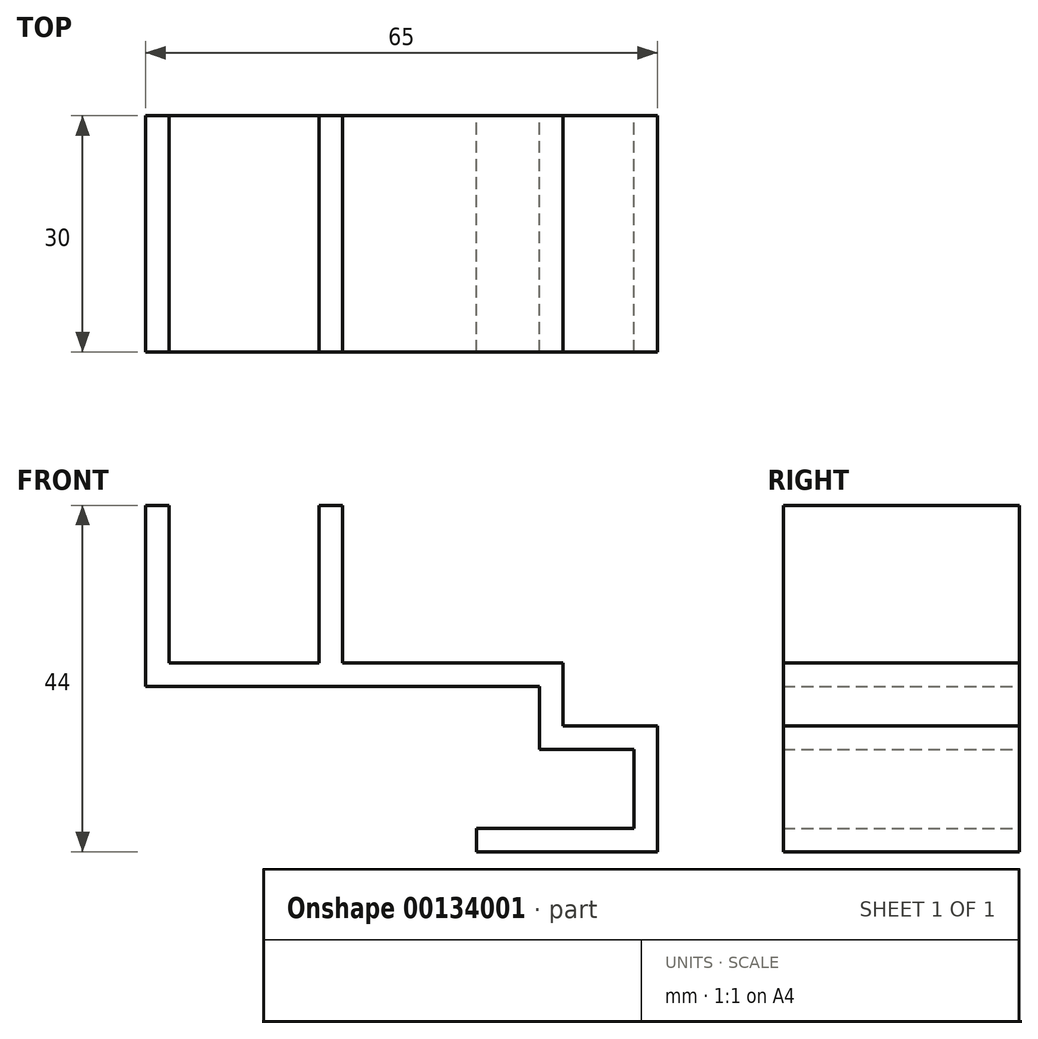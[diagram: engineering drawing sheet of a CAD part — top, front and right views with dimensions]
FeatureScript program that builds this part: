
annotation { "Feature Type Name" : "Feature", "Feature Type Description" : "" }
export const myFeature = defineFeature(function(context is Context, id is Id, definition is map)
    precondition{}
    {
        {
            var Q0;
            Q0=qCreatedBy(makeId("Front.planeOp"),FACE);
            var sketch = newSketch(context, id + "F0", { "sketchPlane" : qUnion([Q0])});
            skLineSegment(sketch, "E0.bottom", {"start": v(0, 0) * mm, "end": v(3, 0) * mm});
            skLineSegment(sketch, "E0.top", {"start": v(0, 23) * mm, "end": v(3, 23) * mm});
            skLineSegment(sketch, "E0.left", {"start": v(0, 0) * mm, "end": v(0, 23) * mm});
            skLineSegment(sketch, "E0.right", {"start": v(3, 0) * mm, "end": v(3, 23) * mm});
            skLineSegment(sketch, "E1.bottom", {"start": v(0, 0) * mm, "end": v(50, 0) * mm});
            skLineSegment(sketch, "E1.top", {"start": v(0, 3) * mm, "end": v(50, 3) * mm});
            skLineSegment(sketch, "E1.left", {"start": v(0, 0) * mm, "end": v(0, 3) * mm});
            skLineSegment(sketch, "E1.right", {"start": v(50, 0) * mm, "end": v(50, 3) * mm});
            skLineSegment(sketch, "E2.bottom", {"start": v(50, 3) * mm, "end": v(53, 3) * mm});
            skLineSegment(sketch, "E2.top", {"start": v(50, -8) * mm, "end": v(53, -8) * mm});
            skLineSegment(sketch, "E2.left", {"start": v(50, 3) * mm, "end": v(50, -8) * mm});
            skLineSegment(sketch, "E2.right", {"start": v(53, 3) * mm, "end": v(53, -8) * mm});
            skPoint(sketch, "E3", {"position": v(53, 0) * mm});
            skLineSegment(sketch, "E4.bottom", {"start": v(50, -8) * mm, "end": v(65, -8) * mm});
            skLineSegment(sketch, "E4.top", {"start": v(50, -5) * mm, "end": v(65, -5) * mm});
            skLineSegment(sketch, "E4.left", {"start": v(50, -8) * mm, "end": v(50, -5) * mm});
            skLineSegment(sketch, "E4.right", {"start": v(65, -8) * mm, "end": v(65, -5) * mm});
            skPoint(sketch, "E5", {"position": v(53, -5) * mm});
            skLineSegment(sketch, "E6.bottom", {"start": v(65, -5) * mm, "end": v(62, -5) * mm});
            skLineSegment(sketch, "E6.top", {"start": v(65, -18) * mm, "end": v(62, -18) * mm});
            skLineSegment(sketch, "E6.left", {"start": v(65, -5) * mm, "end": v(65, -18) * mm});
            skLineSegment(sketch, "E6.right", {"start": v(62, -5) * mm, "end": v(62, -18) * mm});
            skLineSegment(sketch, "E7.bottom", {"start": v(65, -18) * mm, "end": v(42, -18) * mm});
            skLineSegment(sketch, "E7.top", {"start": v(65, -21) * mm, "end": v(42, -21) * mm});
            skLineSegment(sketch, "E7.left", {"start": v(65, -18) * mm, "end": v(65, -21) * mm});
            skLineSegment(sketch, "E7.right", {"start": v(42, -18) * mm, "end": v(42, -21) * mm});
            skPoint(sketch, "E8", {"position": v(62, -8) * mm});
            skLineSegment(sketch, "E9.bottom", {"start": v(22, 23) * mm, "end": v(25, 23) * mm});
            skLineSegment(sketch, "E9.top", {"start": v(22, 0) * mm, "end": v(25, 0) * mm});
            skLineSegment(sketch, "E9.left", {"start": v(22, 23) * mm, "end": v(22, 0) * mm});
            skLineSegment(sketch, "E9.right", {"start": v(25, 23) * mm, "end": v(25, 0) * mm});
            skSolve(sketch);
        }
        {
            var Q0;
            Q0 = qSketchRegion(id + "F0", true);
            extrude(context, id + "F1", {"entities" : qUnion([Q0]), "depth" : 15 * mm, "hasSecondDirection" : true, "secondDirectionOppositeDirection" : true, "secondDirectionDepth" : 15 * mm});
        }
    });
